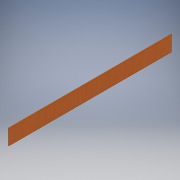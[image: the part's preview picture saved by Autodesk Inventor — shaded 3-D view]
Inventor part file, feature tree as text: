
AUTODESK INVENTOR PART (.ipt)
format: ipt  version: 2016 (Build 200138000, 138)  size: 105,472 bytes
history: native  units: in
note: dims shown in document units (in); Inventor stores cm internally (conversion verified against a paired STEP export)
features: extrude x1, fillet x1, sketch x1
ambient origin geometry x8: Origin, YZ Plane, XZ Plane, XY Plane, X Axis, Y Axis, Z Axis, Center Point
bodies: Solid1 (feature_tree)
feature tree (3):
  extrude  "Extrusion1"  Depth=6.5in
  fillet  "Fillet1"  Radius=0.4375in
  sketch  "Sketch1"  dims[d0=69.0in d1=6.5in d2=0.4375in d3=0.0in d4=0.125in]
